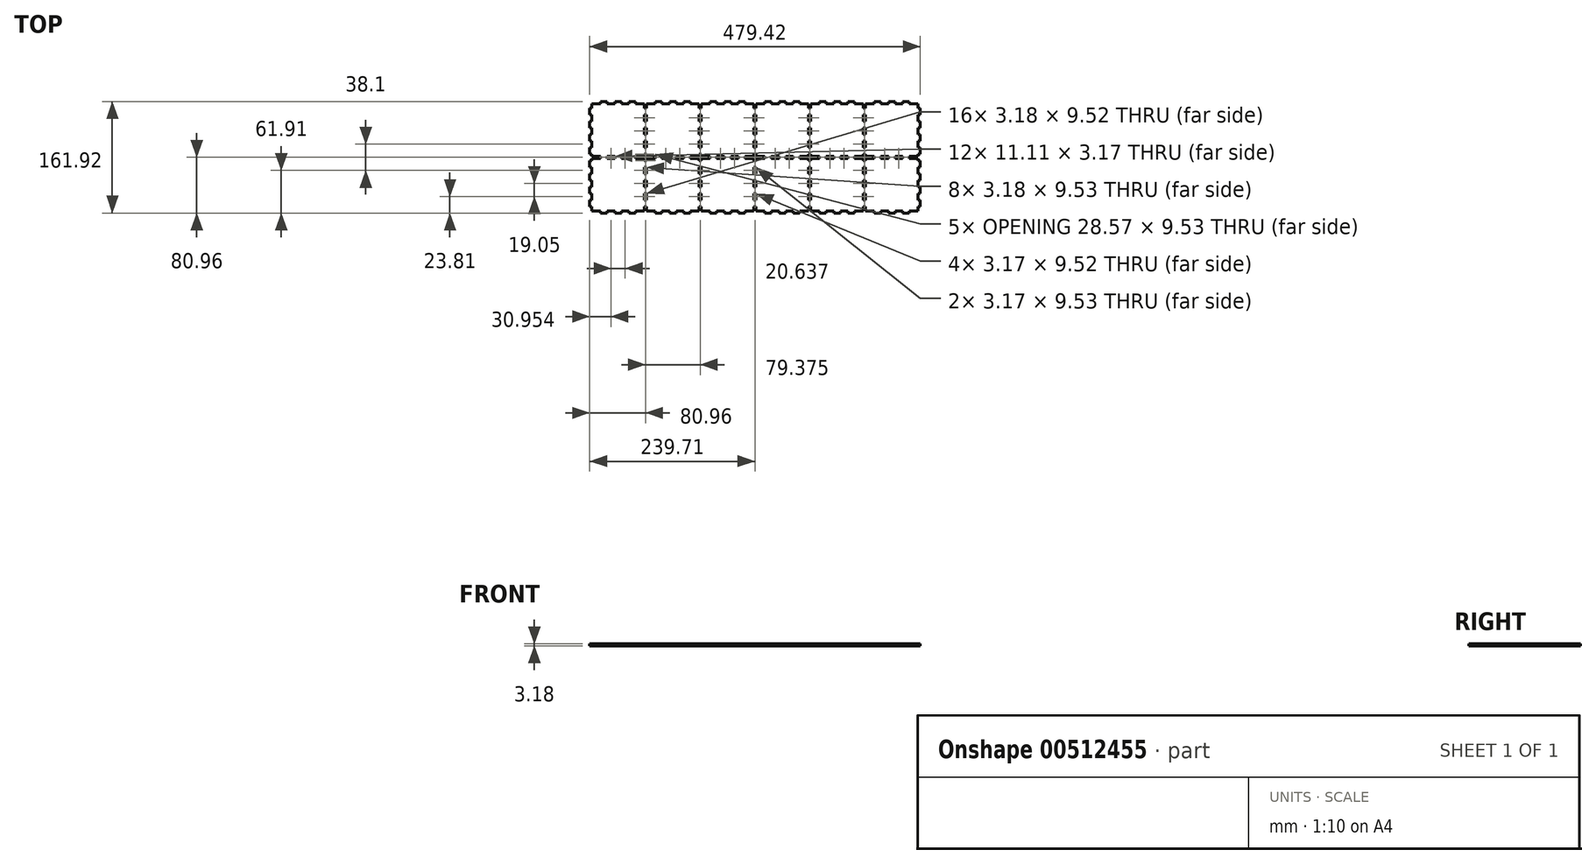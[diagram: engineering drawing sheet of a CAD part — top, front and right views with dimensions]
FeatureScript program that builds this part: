
annotation { "Feature Type Name" : "Feature", "Feature Type Description" : "" }
export const myFeature = defineFeature(function(context is Context, id is Id, definition is map)
    precondition{}
    {
        {
            var Q0;
            Q0=qCreatedBy(makeId("Top.planeOp"),FACE);
            var sketch = newSketch(context, id + "F0", { "sketchPlane" : qUnion([Q0])});
            skLineSegment(sketch, "E0.bottom", {"start": v(-239.71, 80.96) * mm, "end": v(239.71, 80.96) * mm});
            skLineSegment(sketch, "E0.top", {"start": v(-239.71, -80.96) * mm, "end": v(239.71, -80.96) * mm});
            skLineSegment(sketch, "E0.left", {"start": v(-239.71, 80.96) * mm, "end": v(-239.71, -80.96) * mm});
            skLineSegment(sketch, "E0.right", {"start": v(239.71, 80.96) * mm, "end": v(239.71, -80.96) * mm});
            skSolve(sketch);
        }
        {
            var Q0;
            Q0 = qSketchRegion(id + "F0", true);
            extrude(context, id + "F1", {"entities" : qUnion([Q0]), "depth" : 3.17 * mm});
        }
        {
            var Q0;
            Q0=makeQuery(id+"F1.opExtrude","CAP_FACE",FACE,{"disambiguationData":[OSD([sQuery(id+"F0.wireOp",EDGE,"E0.bottom"),sQuery(id+"F0.wireOp",EDGE,"E0.top"),sQuery(id+"F0.wireOp",EDGE,"E0.left"),sQuery(id+"F0.wireOp",EDGE,"E0.right")])],"isStart":false});
            var sketch = newSketch(context, id + "F2", { "sketchPlane" : qUnion([Q0])});
            skLineSegment(sketch, "E1.bottom", {"start": v(-239.71, 80.96) * mm, "end": v(-236.54, 80.96) * mm});
            skLineSegment(sketch, "E1.top", {"start": v(-239.71, 71.44) * mm, "end": v(-236.54, 71.44) * mm});
            skLineSegment(sketch, "E1.left", {"start": v(-239.71, 80.96) * mm, "end": v(-239.71, 71.44) * mm});
            skLineSegment(sketch, "E1.right", {"start": v(-236.54, 80.96) * mm, "end": v(-236.54, 71.44) * mm});
            skLineSegment(sketch, "E2.0.1.0", {"start": v(-239.71, 61.91) * mm, "end": v(-239.71, 52.39) * mm});
            skLineSegment(sketch, "E2.0.1.1", {"start": v(-236.54, 61.91) * mm, "end": v(-236.54, 52.39) * mm});
            skLineSegment(sketch, "E2.0.1.2", {"start": v(-239.71, 61.91) * mm, "end": v(-236.54, 61.91) * mm});
            skLineSegment(sketch, "E2.0.1.3", {"start": v(-239.71, 52.39) * mm, "end": v(-236.54, 52.39) * mm});
            skLineSegment(sketch, "E2.0.2.0", {"start": v(-239.71, 42.86) * mm, "end": v(-239.71, 33.34) * mm});
            skLineSegment(sketch, "E2.0.2.1", {"start": v(-236.54, 42.86) * mm, "end": v(-236.54, 33.34) * mm});
            skLineSegment(sketch, "E2.0.2.2", {"start": v(-239.71, 42.86) * mm, "end": v(-236.54, 42.86) * mm});
            skLineSegment(sketch, "E2.0.2.3", {"start": v(-239.71, 33.34) * mm, "end": v(-236.54, 33.34) * mm});
            skLineSegment(sketch, "E2.0.3.0", {"start": v(-239.71, 23.81) * mm, "end": v(-239.71, 14.29) * mm});
            skLineSegment(sketch, "E2.0.3.1", {"start": v(-236.54, 23.81) * mm, "end": v(-236.54, 14.29) * mm});
            skLineSegment(sketch, "E2.0.3.2", {"start": v(-239.71, 23.81) * mm, "end": v(-236.54, 23.81) * mm});
            skLineSegment(sketch, "E2.0.3.3", {"start": v(-239.71, 14.29) * mm, "end": v(-236.54, 14.29) * mm});
            skLineSegment(sketch, "E2.0.4.0", {"start": v(-239.71, 4.76) * mm, "end": v(-239.71, -4.76) * mm});
            skLineSegment(sketch, "E2.0.4.1", {"start": v(-236.54, 4.76) * mm, "end": v(-236.54, -4.76) * mm});
            skLineSegment(sketch, "E2.0.4.2", {"start": v(-239.71, 4.76) * mm, "end": v(-236.54, 4.76) * mm});
            skLineSegment(sketch, "E2.0.4.3", {"start": v(-239.71, -4.76) * mm, "end": v(-236.54, -4.76) * mm});
            skLineSegment(sketch, "E2.0.5.0", {"start": v(-239.71, -14.29) * mm, "end": v(-239.71, -23.81) * mm});
            skLineSegment(sketch, "E2.0.5.1", {"start": v(-236.54, -14.29) * mm, "end": v(-236.54, -23.81) * mm});
            skLineSegment(sketch, "E2.0.5.2", {"start": v(-239.71, -14.29) * mm, "end": v(-236.54, -14.29) * mm});
            skLineSegment(sketch, "E2.0.5.3", {"start": v(-239.71, -23.81) * mm, "end": v(-236.54, -23.81) * mm});
            skLineSegment(sketch, "E2.0.6.0", {"start": v(-239.71, -33.34) * mm, "end": v(-239.71, -42.86) * mm});
            skLineSegment(sketch, "E2.0.6.1", {"start": v(-236.54, -33.34) * mm, "end": v(-236.54, -42.86) * mm});
            skLineSegment(sketch, "E2.0.6.2", {"start": v(-239.71, -33.34) * mm, "end": v(-236.54, -33.34) * mm});
            skLineSegment(sketch, "E2.0.6.3", {"start": v(-239.71, -42.86) * mm, "end": v(-236.54, -42.86) * mm});
            skLineSegment(sketch, "E2.0.7.0", {"start": v(-239.71, -52.39) * mm, "end": v(-239.71, -61.91) * mm});
            skLineSegment(sketch, "E2.0.7.1", {"start": v(-236.54, -52.39) * mm, "end": v(-236.54, -61.91) * mm});
            skLineSegment(sketch, "E2.0.7.2", {"start": v(-239.71, -52.39) * mm, "end": v(-236.54, -52.39) * mm});
            skLineSegment(sketch, "E2.0.7.3", {"start": v(-239.71, -61.91) * mm, "end": v(-236.54, -61.91) * mm});
            skLineSegment(sketch, "E2.0.8.0", {"start": v(-239.71, -71.44) * mm, "end": v(-239.71, -80.96) * mm});
            skLineSegment(sketch, "E2.0.8.1", {"start": v(-236.54, -71.44) * mm, "end": v(-236.54, -80.96) * mm});
            skLineSegment(sketch, "E2.0.8.2", {"start": v(-239.71, -71.44) * mm, "end": v(-236.54, -71.44) * mm});
            skLineSegment(sketch, "E2.0.8.3", {"start": v(-239.71, -80.96) * mm, "end": v(-236.54, -80.96) * mm});
            skLineSegment(sketch, "E2.direction1", {"start": v(-538.16, 71.44) * mm, "end": v(-239.71, 71.44) * mm, "construction": true});
            skLineSegment(sketch, "E2.direction2", {"start": v(-239.71, 71.44) * mm, "end": v(-239.71, 52.39) * mm, "construction": true});
            skLineSegment(sketch, "E3.1.0.0", {"start": v(-458.79, 71.44) * mm, "end": v(-160.34, 71.44) * mm, "construction": true});
            skLineSegment(sketch, "E3.1.0.1", {"start": v(-160.34, -23.81) * mm, "end": v(-157.16, -23.81) * mm});
            skLineSegment(sketch, "E3.1.0.2", {"start": v(-160.34, -42.86) * mm, "end": v(-157.16, -42.86) * mm});
            skLineSegment(sketch, "E3.1.0.3", {"start": v(-160.34, -14.29) * mm, "end": v(-160.34, -23.81) * mm});
            skLineSegment(sketch, "E3.1.0.4", {"start": v(-157.16, -52.39) * mm, "end": v(-157.16, -61.91) * mm});
            skLineSegment(sketch, "E3.1.0.5", {"start": v(-160.34, -71.44) * mm, "end": v(-160.34, -80.96) * mm});
            skLineSegment(sketch, "E3.1.0.6", {"start": v(-160.34, 4.76) * mm, "end": v(-160.34, -4.76) * mm});
            skLineSegment(sketch, "E3.1.0.7", {"start": v(-160.34, -52.39) * mm, "end": v(-160.34, -61.91) * mm});
            skLineSegment(sketch, "E3.1.0.8", {"start": v(-160.34, -33.34) * mm, "end": v(-160.34, -42.86) * mm});
            skLineSegment(sketch, "E3.1.0.9", {"start": v(-160.34, -52.39) * mm, "end": v(-157.16, -52.39) * mm});
            skLineSegment(sketch, "E3.1.0.10", {"start": v(-160.34, 71.44) * mm, "end": v(-160.34, 52.39) * mm, "construction": true});
            skLineSegment(sketch, "E3.1.0.11", {"start": v(-157.16, -14.29) * mm, "end": v(-157.16, -23.81) * mm});
            skLineSegment(sketch, "E3.1.0.12", {"start": v(-157.16, -71.44) * mm, "end": v(-157.16, -80.96) * mm});
            skLineSegment(sketch, "E3.1.0.13", {"start": v(-157.16, 4.76) * mm, "end": v(-157.16, -4.76) * mm});
            skLineSegment(sketch, "E3.1.0.14", {"start": v(-157.16, 23.81) * mm, "end": v(-157.16, 14.29) * mm});
            skLineSegment(sketch, "E3.1.0.15", {"start": v(-160.34, 23.81) * mm, "end": v(-157.16, 23.81) * mm});
            skLineSegment(sketch, "E3.1.0.16", {"start": v(-160.34, 14.29) * mm, "end": v(-157.16, 14.29) * mm});
            skLineSegment(sketch, "E3.1.0.17", {"start": v(-160.34, 80.96) * mm, "end": v(-157.16, 80.96) * mm});
            skLineSegment(sketch, "E3.1.0.18", {"start": v(-160.34, 80.96) * mm, "end": v(-160.34, 71.44) * mm});
            skLineSegment(sketch, "E3.1.0.19", {"start": v(-157.16, 80.96) * mm, "end": v(-157.16, 71.44) * mm});
            skLineSegment(sketch, "E3.1.0.20", {"start": v(-157.16, 61.91) * mm, "end": v(-157.16, 52.39) * mm});
            skLineSegment(sketch, "E3.1.0.21", {"start": v(-160.34, 61.91) * mm, "end": v(-157.16, 61.91) * mm});
            skLineSegment(sketch, "E3.1.0.22", {"start": v(-160.34, 42.86) * mm, "end": v(-160.34, 33.34) * mm});
            skLineSegment(sketch, "E3.1.0.23", {"start": v(-157.16, 42.86) * mm, "end": v(-157.16, 33.34) * mm});
            skLineSegment(sketch, "E3.1.0.24", {"start": v(-160.34, 42.86) * mm, "end": v(-157.16, 42.86) * mm});
            skLineSegment(sketch, "E3.1.0.25", {"start": v(-160.34, 33.34) * mm, "end": v(-157.16, 33.34) * mm});
            skLineSegment(sketch, "E3.1.0.26", {"start": v(-157.16, -33.34) * mm, "end": v(-157.16, -42.86) * mm});
            skLineSegment(sketch, "E3.1.0.27", {"start": v(-160.34, 23.81) * mm, "end": v(-160.34, 14.29) * mm});
            skLineSegment(sketch, "E3.1.0.28", {"start": v(-160.34, -61.91) * mm, "end": v(-157.16, -61.91) * mm});
            skLineSegment(sketch, "E3.1.0.29", {"start": v(-160.34, -14.29) * mm, "end": v(-157.16, -14.29) * mm});
            skLineSegment(sketch, "E3.1.0.30", {"start": v(-160.34, -71.44) * mm, "end": v(-157.16, -71.44) * mm});
            skLineSegment(sketch, "E3.1.0.31", {"start": v(-160.34, 4.76) * mm, "end": v(-157.16, 4.76) * mm});
            skLineSegment(sketch, "E3.1.0.32", {"start": v(-160.34, -33.34) * mm, "end": v(-157.16, -33.34) * mm});
            skLineSegment(sketch, "E3.1.0.33", {"start": v(-160.34, -80.96) * mm, "end": v(-157.16, -80.96) * mm});
            skLineSegment(sketch, "E3.1.0.34", {"start": v(-160.34, -4.76) * mm, "end": v(-157.16, -4.76) * mm});
            skLineSegment(sketch, "E3.1.0.35", {"start": v(-160.34, 61.91) * mm, "end": v(-160.34, 52.39) * mm});
            skLineSegment(sketch, "E3.1.0.36", {"start": v(-160.34, 52.39) * mm, "end": v(-157.16, 52.39) * mm});
            skLineSegment(sketch, "E3.1.0.37", {"start": v(-160.34, 71.44) * mm, "end": v(-157.16, 71.44) * mm});
            skLineSegment(sketch, "E3.2.0.0", {"start": v(-379.41, 71.44) * mm, "end": v(-80.96, 71.44) * mm, "construction": true});
            skLineSegment(sketch, "E3.2.0.1", {"start": v(-80.96, -23.81) * mm, "end": v(-77.79, -23.81) * mm});
            skLineSegment(sketch, "E3.2.0.2", {"start": v(-80.96, -42.86) * mm, "end": v(-77.79, -42.86) * mm});
            skLineSegment(sketch, "E3.2.0.3", {"start": v(-80.96, -14.29) * mm, "end": v(-80.96, -23.81) * mm});
            skLineSegment(sketch, "E3.2.0.4", {"start": v(-77.79, -52.39) * mm, "end": v(-77.79, -61.91) * mm});
            skLineSegment(sketch, "E3.2.0.5", {"start": v(-80.96, -71.44) * mm, "end": v(-80.96, -80.96) * mm});
            skLineSegment(sketch, "E3.2.0.6", {"start": v(-80.96, 4.76) * mm, "end": v(-80.96, -4.76) * mm});
            skLineSegment(sketch, "E3.2.0.7", {"start": v(-80.96, -52.39) * mm, "end": v(-80.96, -61.91) * mm});
            skLineSegment(sketch, "E3.2.0.8", {"start": v(-80.96, -33.34) * mm, "end": v(-80.96, -42.86) * mm});
            skLineSegment(sketch, "E3.2.0.9", {"start": v(-80.96, -52.39) * mm, "end": v(-77.79, -52.39) * mm});
            skLineSegment(sketch, "E3.2.0.10", {"start": v(-80.96, 71.44) * mm, "end": v(-80.96, 52.39) * mm, "construction": true});
            skLineSegment(sketch, "E3.2.0.11", {"start": v(-77.79, -14.29) * mm, "end": v(-77.79, -23.81) * mm});
            skLineSegment(sketch, "E3.2.0.12", {"start": v(-77.79, -71.44) * mm, "end": v(-77.79, -80.96) * mm});
            skLineSegment(sketch, "E3.2.0.13", {"start": v(-77.79, 4.76) * mm, "end": v(-77.79, -4.76) * mm});
            skLineSegment(sketch, "E3.2.0.14", {"start": v(-77.79, 23.81) * mm, "end": v(-77.79, 14.29) * mm});
            skLineSegment(sketch, "E3.2.0.15", {"start": v(-80.96, 23.81) * mm, "end": v(-77.79, 23.81) * mm});
            skLineSegment(sketch, "E3.2.0.16", {"start": v(-80.96, 14.29) * mm, "end": v(-77.79, 14.29) * mm});
            skLineSegment(sketch, "E3.2.0.17", {"start": v(-80.96, 80.96) * mm, "end": v(-77.79, 80.96) * mm});
            skLineSegment(sketch, "E3.2.0.18", {"start": v(-80.96, 80.96) * mm, "end": v(-80.96, 71.44) * mm});
            skLineSegment(sketch, "E3.2.0.19", {"start": v(-77.79, 80.96) * mm, "end": v(-77.79, 71.44) * mm});
            skLineSegment(sketch, "E3.2.0.20", {"start": v(-77.79, 61.91) * mm, "end": v(-77.79, 52.39) * mm});
            skLineSegment(sketch, "E3.2.0.21", {"start": v(-80.96, 61.91) * mm, "end": v(-77.79, 61.91) * mm});
            skLineSegment(sketch, "E3.2.0.22", {"start": v(-80.96, 42.86) * mm, "end": v(-80.96, 33.34) * mm});
            skLineSegment(sketch, "E3.2.0.23", {"start": v(-77.79, 42.86) * mm, "end": v(-77.79, 33.34) * mm});
            skLineSegment(sketch, "E3.2.0.24", {"start": v(-80.96, 42.86) * mm, "end": v(-77.79, 42.86) * mm});
            skLineSegment(sketch, "E3.2.0.25", {"start": v(-80.96, 33.34) * mm, "end": v(-77.79, 33.34) * mm});
            skLineSegment(sketch, "E3.2.0.26", {"start": v(-77.79, -33.34) * mm, "end": v(-77.79, -42.86) * mm});
            skLineSegment(sketch, "E3.2.0.27", {"start": v(-80.96, 23.81) * mm, "end": v(-80.96, 14.29) * mm});
            skLineSegment(sketch, "E3.2.0.28", {"start": v(-80.96, -61.91) * mm, "end": v(-77.79, -61.91) * mm});
            skLineSegment(sketch, "E3.2.0.29", {"start": v(-80.96, -14.29) * mm, "end": v(-77.79, -14.29) * mm});
            skLineSegment(sketch, "E3.2.0.30", {"start": v(-80.96, -71.44) * mm, "end": v(-77.79, -71.44) * mm});
            skLineSegment(sketch, "E3.2.0.31", {"start": v(-80.96, 4.76) * mm, "end": v(-77.79, 4.76) * mm});
            skLineSegment(sketch, "E3.2.0.32", {"start": v(-80.96, -33.34) * mm, "end": v(-77.79, -33.34) * mm});
            skLineSegment(sketch, "E3.2.0.33", {"start": v(-80.96, -80.96) * mm, "end": v(-77.79, -80.96) * mm});
            skLineSegment(sketch, "E3.2.0.34", {"start": v(-80.96, -4.76) * mm, "end": v(-77.79, -4.76) * mm});
            skLineSegment(sketch, "E3.2.0.35", {"start": v(-80.96, 61.91) * mm, "end": v(-80.96, 52.39) * mm});
            skLineSegment(sketch, "E3.2.0.36", {"start": v(-80.96, 52.39) * mm, "end": v(-77.79, 52.39) * mm});
            skLineSegment(sketch, "E3.2.0.37", {"start": v(-80.96, 71.44) * mm, "end": v(-77.79, 71.44) * mm});
            skLineSegment(sketch, "E3.3.0.0", {"start": v(-300.04, 71.44) * mm, "end": v(-1.59, 71.44) * mm, "construction": true});
            skLineSegment(sketch, "E3.3.0.1", {"start": v(-1.59, -23.81) * mm, "end": v(1.59, -23.81) * mm});
            skLineSegment(sketch, "E3.3.0.2", {"start": v(-1.59, -42.86) * mm, "end": v(1.59, -42.86) * mm});
            skLineSegment(sketch, "E3.3.0.3", {"start": v(-1.59, -14.29) * mm, "end": v(-1.59, -23.81) * mm});
            skLineSegment(sketch, "E3.3.0.4", {"start": v(1.59, -52.39) * mm, "end": v(1.59, -61.91) * mm});
            skLineSegment(sketch, "E3.3.0.5", {"start": v(-1.59, -71.44) * mm, "end": v(-1.59, -80.96) * mm});
            skLineSegment(sketch, "E3.3.0.6", {"start": v(-1.59, 4.76) * mm, "end": v(-1.59, -4.76) * mm});
            skLineSegment(sketch, "E3.3.0.7", {"start": v(-1.59, -52.39) * mm, "end": v(-1.59, -61.91) * mm});
            skLineSegment(sketch, "E3.3.0.8", {"start": v(-1.59, -33.34) * mm, "end": v(-1.59, -42.86) * mm});
            skLineSegment(sketch, "E3.3.0.9", {"start": v(-1.59, -52.39) * mm, "end": v(1.59, -52.39) * mm});
            skLineSegment(sketch, "E3.3.0.10", {"start": v(-1.59, 71.44) * mm, "end": v(-1.59, 52.39) * mm, "construction": true});
            skLineSegment(sketch, "E3.3.0.11", {"start": v(1.59, -14.29) * mm, "end": v(1.59, -23.81) * mm});
            skLineSegment(sketch, "E3.3.0.12", {"start": v(1.59, -71.44) * mm, "end": v(1.59, -80.96) * mm});
            skLineSegment(sketch, "E3.3.0.13", {"start": v(1.59, 4.76) * mm, "end": v(1.59, -4.76) * mm});
            skLineSegment(sketch, "E3.3.0.14", {"start": v(1.59, 23.81) * mm, "end": v(1.59, 14.29) * mm});
            skLineSegment(sketch, "E3.3.0.15", {"start": v(-1.59, 23.81) * mm, "end": v(1.59, 23.81) * mm});
            skLineSegment(sketch, "E3.3.0.16", {"start": v(-1.59, 14.29) * mm, "end": v(1.59, 14.29) * mm});
            skLineSegment(sketch, "E3.3.0.17", {"start": v(-1.59, 80.96) * mm, "end": v(1.59, 80.96) * mm});
            skLineSegment(sketch, "E3.3.0.18", {"start": v(-1.59, 80.96) * mm, "end": v(-1.59, 71.44) * mm});
            skLineSegment(sketch, "E3.3.0.19", {"start": v(1.59, 80.96) * mm, "end": v(1.59, 71.44) * mm});
            skLineSegment(sketch, "E3.3.0.20", {"start": v(1.59, 61.91) * mm, "end": v(1.59, 52.39) * mm});
            skLineSegment(sketch, "E3.3.0.21", {"start": v(-1.59, 61.91) * mm, "end": v(1.59, 61.91) * mm});
            skLineSegment(sketch, "E3.3.0.22", {"start": v(-1.59, 42.86) * mm, "end": v(-1.59, 33.34) * mm});
            skLineSegment(sketch, "E3.3.0.23", {"start": v(1.59, 42.86) * mm, "end": v(1.59, 33.34) * mm});
            skLineSegment(sketch, "E3.3.0.24", {"start": v(-1.59, 42.86) * mm, "end": v(1.59, 42.86) * mm});
            skLineSegment(sketch, "E3.3.0.25", {"start": v(-1.59, 33.34) * mm, "end": v(1.59, 33.34) * mm});
            skLineSegment(sketch, "E3.3.0.26", {"start": v(1.59, -33.34) * mm, "end": v(1.59, -42.86) * mm});
            skLineSegment(sketch, "E3.3.0.27", {"start": v(-1.59, 23.81) * mm, "end": v(-1.59, 14.29) * mm});
            skLineSegment(sketch, "E3.3.0.28", {"start": v(-1.59, -61.91) * mm, "end": v(1.59, -61.91) * mm});
            skLineSegment(sketch, "E3.3.0.29", {"start": v(-1.59, -14.29) * mm, "end": v(1.59, -14.29) * mm});
            skLineSegment(sketch, "E3.3.0.30", {"start": v(-1.59, -71.44) * mm, "end": v(1.59, -71.44) * mm});
            skLineSegment(sketch, "E3.3.0.31", {"start": v(-1.59, 4.76) * mm, "end": v(1.59, 4.76) * mm});
            skLineSegment(sketch, "E3.3.0.32", {"start": v(-1.59, -33.34) * mm, "end": v(1.59, -33.34) * mm});
            skLineSegment(sketch, "E3.3.0.33", {"start": v(-1.59, -80.96) * mm, "end": v(1.59, -80.96) * mm});
            skLineSegment(sketch, "E3.3.0.34", {"start": v(-1.59, -4.76) * mm, "end": v(1.59, -4.76) * mm});
            skLineSegment(sketch, "E3.3.0.35", {"start": v(-1.59, 61.91) * mm, "end": v(-1.59, 52.39) * mm});
            skLineSegment(sketch, "E3.3.0.36", {"start": v(-1.59, 52.39) * mm, "end": v(1.59, 52.39) * mm});
            skLineSegment(sketch, "E3.3.0.37", {"start": v(-1.59, 71.44) * mm, "end": v(1.59, 71.44) * mm});
            skLineSegment(sketch, "E3.4.0.0", {"start": v(-220.66, 71.44) * mm, "end": v(77.79, 71.44) * mm, "construction": true});
            skLineSegment(sketch, "E3.4.0.1", {"start": v(77.79, -23.81) * mm, "end": v(80.96, -23.81) * mm});
            skLineSegment(sketch, "E3.4.0.2", {"start": v(77.79, -42.86) * mm, "end": v(80.96, -42.86) * mm});
            skLineSegment(sketch, "E3.4.0.3", {"start": v(77.79, -14.29) * mm, "end": v(77.79, -23.81) * mm});
            skLineSegment(sketch, "E3.4.0.4", {"start": v(80.96, -52.39) * mm, "end": v(80.96, -61.91) * mm});
            skLineSegment(sketch, "E3.4.0.5", {"start": v(77.79, -71.44) * mm, "end": v(77.79, -80.96) * mm});
            skLineSegment(sketch, "E3.4.0.6", {"start": v(77.79, 4.76) * mm, "end": v(77.79, -4.76) * mm});
            skLineSegment(sketch, "E3.4.0.7", {"start": v(77.79, -52.39) * mm, "end": v(77.79, -61.91) * mm});
            skLineSegment(sketch, "E3.4.0.8", {"start": v(77.79, -33.34) * mm, "end": v(77.79, -42.86) * mm});
            skLineSegment(sketch, "E3.4.0.9", {"start": v(77.79, -52.39) * mm, "end": v(80.96, -52.39) * mm});
            skLineSegment(sketch, "E3.4.0.10", {"start": v(77.79, 71.44) * mm, "end": v(77.79, 52.39) * mm, "construction": true});
            skLineSegment(sketch, "E3.4.0.11", {"start": v(80.96, -14.29) * mm, "end": v(80.96, -23.81) * mm});
            skLineSegment(sketch, "E3.4.0.12", {"start": v(80.96, -71.44) * mm, "end": v(80.96, -80.96) * mm});
            skLineSegment(sketch, "E3.4.0.13", {"start": v(80.96, 4.76) * mm, "end": v(80.96, -4.76) * mm});
            skLineSegment(sketch, "E3.4.0.14", {"start": v(80.96, 23.81) * mm, "end": v(80.96, 14.29) * mm});
            skLineSegment(sketch, "E3.4.0.15", {"start": v(77.79, 23.81) * mm, "end": v(80.96, 23.81) * mm});
            skLineSegment(sketch, "E3.4.0.16", {"start": v(77.79, 14.29) * mm, "end": v(80.96, 14.29) * mm});
            skLineSegment(sketch, "E3.4.0.17", {"start": v(77.79, 80.96) * mm, "end": v(80.96, 80.96) * mm});
            skLineSegment(sketch, "E3.4.0.18", {"start": v(77.79, 80.96) * mm, "end": v(77.79, 71.44) * mm});
            skLineSegment(sketch, "E3.4.0.19", {"start": v(80.96, 80.96) * mm, "end": v(80.96, 71.44) * mm});
            skLineSegment(sketch, "E3.4.0.20", {"start": v(80.96, 61.91) * mm, "end": v(80.96, 52.39) * mm});
            skLineSegment(sketch, "E3.4.0.21", {"start": v(77.79, 61.91) * mm, "end": v(80.96, 61.91) * mm});
            skLineSegment(sketch, "E3.4.0.22", {"start": v(77.79, 42.86) * mm, "end": v(77.79, 33.34) * mm});
            skLineSegment(sketch, "E3.4.0.23", {"start": v(80.96, 42.86) * mm, "end": v(80.96, 33.34) * mm});
            skLineSegment(sketch, "E3.4.0.24", {"start": v(77.79, 42.86) * mm, "end": v(80.96, 42.86) * mm});
            skLineSegment(sketch, "E3.4.0.25", {"start": v(77.79, 33.34) * mm, "end": v(80.96, 33.34) * mm});
            skLineSegment(sketch, "E3.4.0.26", {"start": v(80.96, -33.34) * mm, "end": v(80.96, -42.86) * mm});
            skLineSegment(sketch, "E3.4.0.27", {"start": v(77.79, 23.81) * mm, "end": v(77.79, 14.29) * mm});
            skLineSegment(sketch, "E3.4.0.28", {"start": v(77.79, -61.91) * mm, "end": v(80.96, -61.91) * mm});
            skLineSegment(sketch, "E3.4.0.29", {"start": v(77.79, -14.29) * mm, "end": v(80.96, -14.29) * mm});
            skLineSegment(sketch, "E3.4.0.30", {"start": v(77.79, -71.44) * mm, "end": v(80.96, -71.44) * mm});
            skLineSegment(sketch, "E3.4.0.31", {"start": v(77.79, 4.76) * mm, "end": v(80.96, 4.76) * mm});
            skLineSegment(sketch, "E3.4.0.32", {"start": v(77.79, -33.34) * mm, "end": v(80.96, -33.34) * mm});
            skLineSegment(sketch, "E3.4.0.33", {"start": v(77.79, -80.96) * mm, "end": v(80.96, -80.96) * mm});
            skLineSegment(sketch, "E3.4.0.34", {"start": v(77.79, -4.76) * mm, "end": v(80.96, -4.76) * mm});
            skLineSegment(sketch, "E3.4.0.35", {"start": v(77.79, 61.91) * mm, "end": v(77.79, 52.39) * mm});
            skLineSegment(sketch, "E3.4.0.36", {"start": v(77.79, 52.39) * mm, "end": v(80.96, 52.39) * mm});
            skLineSegment(sketch, "E3.4.0.37", {"start": v(77.79, 71.44) * mm, "end": v(80.96, 71.44) * mm});
            skLineSegment(sketch, "E3.5.0.0", {"start": v(-141.29, 71.44) * mm, "end": v(157.16, 71.44) * mm, "construction": true});
            skLineSegment(sketch, "E3.5.0.1", {"start": v(157.16, -23.81) * mm, "end": v(160.34, -23.81) * mm});
            skLineSegment(sketch, "E3.5.0.2", {"start": v(157.16, -42.86) * mm, "end": v(160.34, -42.86) * mm});
            skLineSegment(sketch, "E3.5.0.3", {"start": v(157.16, -14.29) * mm, "end": v(157.16, -23.81) * mm});
            skLineSegment(sketch, "E3.5.0.4", {"start": v(160.34, -52.39) * mm, "end": v(160.34, -61.91) * mm});
            skLineSegment(sketch, "E3.5.0.5", {"start": v(157.16, -71.44) * mm, "end": v(157.16, -80.96) * mm});
            skLineSegment(sketch, "E3.5.0.6", {"start": v(157.16, 4.76) * mm, "end": v(157.16, -4.76) * mm});
            skLineSegment(sketch, "E3.5.0.7", {"start": v(157.16, -52.39) * mm, "end": v(157.16, -61.91) * mm});
            skLineSegment(sketch, "E3.5.0.8", {"start": v(157.16, -33.34) * mm, "end": v(157.16, -42.86) * mm});
            skLineSegment(sketch, "E3.5.0.9", {"start": v(157.16, -52.39) * mm, "end": v(160.34, -52.39) * mm});
            skLineSegment(sketch, "E3.5.0.10", {"start": v(157.16, 71.44) * mm, "end": v(157.16, 52.39) * mm, "construction": true});
            skLineSegment(sketch, "E3.5.0.11", {"start": v(160.34, -14.29) * mm, "end": v(160.34, -23.81) * mm});
            skLineSegment(sketch, "E3.5.0.12", {"start": v(160.34, -71.44) * mm, "end": v(160.34, -80.96) * mm});
            skLineSegment(sketch, "E3.5.0.13", {"start": v(160.34, 4.76) * mm, "end": v(160.34, -4.76) * mm});
            skLineSegment(sketch, "E3.5.0.14", {"start": v(160.34, 23.81) * mm, "end": v(160.34, 14.29) * mm});
            skLineSegment(sketch, "E3.5.0.15", {"start": v(157.16, 23.81) * mm, "end": v(160.34, 23.81) * mm});
            skLineSegment(sketch, "E3.5.0.16", {"start": v(157.16, 14.29) * mm, "end": v(160.34, 14.29) * mm});
            skLineSegment(sketch, "E3.5.0.17", {"start": v(157.16, 80.96) * mm, "end": v(160.34, 80.96) * mm});
            skLineSegment(sketch, "E3.5.0.18", {"start": v(157.16, 80.96) * mm, "end": v(157.16, 71.44) * mm});
            skLineSegment(sketch, "E3.5.0.19", {"start": v(160.34, 80.96) * mm, "end": v(160.34, 71.44) * mm});
            skLineSegment(sketch, "E3.5.0.20", {"start": v(160.34, 61.91) * mm, "end": v(160.34, 52.39) * mm});
            skLineSegment(sketch, "E3.5.0.21", {"start": v(157.16, 61.91) * mm, "end": v(160.34, 61.91) * mm});
            skLineSegment(sketch, "E3.5.0.22", {"start": v(157.16, 42.86) * mm, "end": v(157.16, 33.34) * mm});
            skLineSegment(sketch, "E3.5.0.23", {"start": v(160.34, 42.86) * mm, "end": v(160.34, 33.34) * mm});
            skLineSegment(sketch, "E3.5.0.24", {"start": v(157.16, 42.86) * mm, "end": v(160.34, 42.86) * mm});
            skLineSegment(sketch, "E3.5.0.25", {"start": v(157.16, 33.34) * mm, "end": v(160.34, 33.34) * mm});
            skLineSegment(sketch, "E3.5.0.26", {"start": v(160.34, -33.34) * mm, "end": v(160.34, -42.86) * mm});
            skLineSegment(sketch, "E3.5.0.27", {"start": v(157.16, 23.81) * mm, "end": v(157.16, 14.29) * mm});
            skLineSegment(sketch, "E3.5.0.28", {"start": v(157.16, -61.91) * mm, "end": v(160.34, -61.91) * mm});
            skLineSegment(sketch, "E3.5.0.29", {"start": v(157.16, -14.29) * mm, "end": v(160.34, -14.29) * mm});
            skLineSegment(sketch, "E3.5.0.30", {"start": v(157.16, -71.44) * mm, "end": v(160.34, -71.44) * mm});
            skLineSegment(sketch, "E3.5.0.31", {"start": v(157.16, 4.76) * mm, "end": v(160.34, 4.76) * mm});
            skLineSegment(sketch, "E3.5.0.32", {"start": v(157.16, -33.34) * mm, "end": v(160.34, -33.34) * mm});
            skLineSegment(sketch, "E3.5.0.33", {"start": v(157.16, -80.96) * mm, "end": v(160.34, -80.96) * mm});
            skLineSegment(sketch, "E3.5.0.34", {"start": v(157.16, -4.76) * mm, "end": v(160.34, -4.76) * mm});
            skLineSegment(sketch, "E3.5.0.35", {"start": v(157.16, 61.91) * mm, "end": v(157.16, 52.39) * mm});
            skLineSegment(sketch, "E3.5.0.36", {"start": v(157.16, 52.39) * mm, "end": v(160.34, 52.39) * mm});
            skLineSegment(sketch, "E3.5.0.37", {"start": v(157.16, 71.44) * mm, "end": v(160.34, 71.44) * mm});
            skLineSegment(sketch, "E3.6.0.0", {"start": v(-61.91, 71.44) * mm, "end": v(236.54, 71.44) * mm, "construction": true});
            skLineSegment(sketch, "E3.6.0.1", {"start": v(236.54, -23.81) * mm, "end": v(239.71, -23.81) * mm});
            skLineSegment(sketch, "E3.6.0.2", {"start": v(236.54, -42.86) * mm, "end": v(239.71, -42.86) * mm});
            skLineSegment(sketch, "E3.6.0.3", {"start": v(236.54, -14.29) * mm, "end": v(236.54, -23.81) * mm});
            skLineSegment(sketch, "E3.6.0.4", {"start": v(239.71, -52.39) * mm, "end": v(239.71, -61.91) * mm});
            skLineSegment(sketch, "E3.6.0.5", {"start": v(236.54, -71.44) * mm, "end": v(236.54, -80.96) * mm});
            skLineSegment(sketch, "E3.6.0.6", {"start": v(236.54, 4.76) * mm, "end": v(236.54, -4.76) * mm});
            skLineSegment(sketch, "E3.6.0.7", {"start": v(236.54, -52.39) * mm, "end": v(236.54, -61.91) * mm});
            skLineSegment(sketch, "E3.6.0.8", {"start": v(236.54, -33.34) * mm, "end": v(236.54, -42.86) * mm});
            skLineSegment(sketch, "E3.6.0.9", {"start": v(236.54, -52.39) * mm, "end": v(239.71, -52.39) * mm});
            skLineSegment(sketch, "E3.6.0.10", {"start": v(236.54, 71.44) * mm, "end": v(236.54, 52.39) * mm, "construction": true});
            skLineSegment(sketch, "E3.6.0.11", {"start": v(239.71, -14.29) * mm, "end": v(239.71, -23.81) * mm});
            skLineSegment(sketch, "E3.6.0.12", {"start": v(239.71, -71.44) * mm, "end": v(239.71, -80.96) * mm});
            skLineSegment(sketch, "E3.6.0.13", {"start": v(239.71, 4.76) * mm, "end": v(239.71, -4.76) * mm});
            skLineSegment(sketch, "E3.6.0.14", {"start": v(239.71, 23.81) * mm, "end": v(239.71, 14.29) * mm});
            skLineSegment(sketch, "E3.6.0.15", {"start": v(236.54, 23.81) * mm, "end": v(239.71, 23.81) * mm});
            skLineSegment(sketch, "E3.6.0.16", {"start": v(236.54, 14.29) * mm, "end": v(239.71, 14.29) * mm});
            skLineSegment(sketch, "E3.6.0.17", {"start": v(236.54, 80.96) * mm, "end": v(239.71, 80.96) * mm});
            skLineSegment(sketch, "E3.6.0.18", {"start": v(236.54, 80.96) * mm, "end": v(236.54, 71.44) * mm});
            skLineSegment(sketch, "E3.6.0.19", {"start": v(239.71, 80.96) * mm, "end": v(239.71, 71.44) * mm});
            skLineSegment(sketch, "E3.6.0.20", {"start": v(239.71, 61.91) * mm, "end": v(239.71, 52.39) * mm});
            skLineSegment(sketch, "E3.6.0.21", {"start": v(236.54, 61.91) * mm, "end": v(239.71, 61.91) * mm});
            skLineSegment(sketch, "E3.6.0.22", {"start": v(236.54, 42.86) * mm, "end": v(236.54, 33.34) * mm});
            skLineSegment(sketch, "E3.6.0.23", {"start": v(239.71, 42.86) * mm, "end": v(239.71, 33.34) * mm});
            skLineSegment(sketch, "E3.6.0.24", {"start": v(236.54, 42.86) * mm, "end": v(239.71, 42.86) * mm});
            skLineSegment(sketch, "E3.6.0.25", {"start": v(236.54, 33.34) * mm, "end": v(239.71, 33.34) * mm});
            skLineSegment(sketch, "E3.6.0.26", {"start": v(239.71, -33.34) * mm, "end": v(239.71, -42.86) * mm});
            skLineSegment(sketch, "E3.6.0.27", {"start": v(236.54, 23.81) * mm, "end": v(236.54, 14.29) * mm});
            skLineSegment(sketch, "E3.6.0.28", {"start": v(236.54, -61.91) * mm, "end": v(239.71, -61.91) * mm});
            skLineSegment(sketch, "E3.6.0.29", {"start": v(236.54, -14.29) * mm, "end": v(239.71, -14.29) * mm});
            skLineSegment(sketch, "E3.6.0.30", {"start": v(236.54, -71.44) * mm, "end": v(239.71, -71.44) * mm});
            skLineSegment(sketch, "E3.6.0.31", {"start": v(236.54, 4.76) * mm, "end": v(239.71, 4.76) * mm});
            skLineSegment(sketch, "E3.6.0.32", {"start": v(236.54, -33.34) * mm, "end": v(239.71, -33.34) * mm});
            skLineSegment(sketch, "E3.6.0.33", {"start": v(236.54, -80.96) * mm, "end": v(239.71, -80.96) * mm});
            skLineSegment(sketch, "E3.6.0.34", {"start": v(236.54, -4.76) * mm, "end": v(239.71, -4.76) * mm});
            skLineSegment(sketch, "E3.6.0.35", {"start": v(236.54, 61.91) * mm, "end": v(236.54, 52.39) * mm});
            skLineSegment(sketch, "E3.6.0.36", {"start": v(236.54, 52.39) * mm, "end": v(239.71, 52.39) * mm});
            skLineSegment(sketch, "E3.6.0.37", {"start": v(236.54, 71.44) * mm, "end": v(239.71, 71.44) * mm});
            skLineSegment(sketch, "E3.direction1", {"start": v(-239.71, -80.96) * mm, "end": v(-160.34, -80.96) * mm, "construction": true});
            skSolve(sketch);
        }
        {
            var Q0;
            Q0 = qSketchRegion(id + "F2", true);
            extrude(context, id + "F3", {"entities" : qUnion([Q0]), "operationType" : NewBodyOperationType.REMOVE, "endBound" : BoundingType.THROUGH_ALL, "oppositeDirection" : true, "depth" : 25.4 * mm});
        }
        {
            var Q0;
            Q0=makeQuery(id+"F1.opExtrude","CAP_FACE",FACE,{"disambiguationData":[OSD([sQuery(id+"F0.wireOp",EDGE,"E0.bottom"),sQuery(id+"F0.wireOp",EDGE,"E0.top"),sQuery(id+"F0.wireOp",EDGE,"E0.left"),sQuery(id+"F0.wireOp",EDGE,"E0.right")])],"isStart":false});
            var sketch = newSketch(context, id + "F4", { "sketchPlane" : qUnion([Q0])});
            skLineSegment(sketch, "E4.bottom", {"start": v(-236.54, 80.96) * mm, "end": v(-223.84, 80.96) * mm});
            skLineSegment(sketch, "E4.top", {"start": v(-236.54, 77.79) * mm, "end": v(-223.84, 77.79) * mm});
            skLineSegment(sketch, "E4.left", {"start": v(-236.54, 80.96) * mm, "end": v(-236.54, 77.79) * mm});
            skLineSegment(sketch, "E4.right", {"start": v(-223.84, 80.96) * mm, "end": v(-223.84, 77.79) * mm});
            skLineSegment(sketch, "E5.bottom", {"start": v(-214.31, 80.96) * mm, "end": v(-203.2, 80.96) * mm});
            skLineSegment(sketch, "E5.top", {"start": v(-214.31, 77.79) * mm, "end": v(-203.2, 77.79) * mm});
            skLineSegment(sketch, "E5.left", {"start": v(-214.31, 80.96) * mm, "end": v(-214.31, 77.79) * mm});
            skLineSegment(sketch, "E5.right", {"start": v(-203.2, 80.96) * mm, "end": v(-203.2, 77.79) * mm});
            skLineSegment(sketch, "E6.1.0.0", {"start": v(-193.68, 77.79) * mm, "end": v(-182.56, 77.79) * mm});
            skLineSegment(sketch, "E6.1.0.1", {"start": v(-182.56, 80.96) * mm, "end": v(-182.56, 77.79) * mm});
            skLineSegment(sketch, "E6.1.0.2", {"start": v(-193.68, 80.96) * mm, "end": v(-193.68, 77.79) * mm});
            skLineSegment(sketch, "E6.1.0.3", {"start": v(-193.68, 80.96) * mm, "end": v(-182.56, 80.96) * mm});
            skLineSegment(sketch, "E6.direction1", {"start": v(-214.31, 77.79) * mm, "end": v(-193.68, 77.79) * mm, "construction": true});
            skLineSegment(sketch, "E7.bottom", {"start": v(-160.34, 80.96) * mm, "end": v(-173.04, 80.96) * mm});
            skLineSegment(sketch, "E7.top", {"start": v(-160.34, 77.79) * mm, "end": v(-173.04, 77.79) * mm});
            skLineSegment(sketch, "E7.left", {"start": v(-160.34, 80.96) * mm, "end": v(-160.34, 77.79) * mm});
            skLineSegment(sketch, "E7.right", {"start": v(-173.04, 80.96) * mm, "end": v(-173.04, 77.79) * mm});
            skLineSegment(sketch, "E8.0.1.0", {"start": v(-214.31, 1.59) * mm, "end": v(-203.2, 1.59) * mm});
            skLineSegment(sketch, "E8.0.1.1", {"start": v(-193.68, -1.59) * mm, "end": v(-182.56, -1.59) * mm});
            skLineSegment(sketch, "E8.0.1.2", {"start": v(-214.31, -1.59) * mm, "end": v(-193.68, -1.59) * mm, "construction": true});
            skLineSegment(sketch, "E8.0.1.3", {"start": v(-193.68, 1.59) * mm, "end": v(-182.56, 1.59) * mm});
            skLineSegment(sketch, "E8.0.1.4", {"start": v(-160.34, -1.59) * mm, "end": v(-173.04, -1.59) * mm});
            skLineSegment(sketch, "E8.0.1.5", {"start": v(-236.54, -1.59) * mm, "end": v(-223.84, -1.59) * mm});
            skLineSegment(sketch, "E8.0.1.6", {"start": v(-236.54, 1.59) * mm, "end": v(-223.84, 1.59) * mm});
            skLineSegment(sketch, "E8.0.1.7", {"start": v(-160.34, 1.59) * mm, "end": v(-173.04, 1.59) * mm});
            skLineSegment(sketch, "E8.0.1.8", {"start": v(-214.31, -1.59) * mm, "end": v(-203.2, -1.59) * mm});
            skLineSegment(sketch, "E8.0.1.9", {"start": v(-203.2, 1.59) * mm, "end": v(-203.2, -1.59) * mm});
            skLineSegment(sketch, "E8.0.1.10", {"start": v(-193.68, 1.59) * mm, "end": v(-193.68, -1.59) * mm});
            skLineSegment(sketch, "E8.0.1.11", {"start": v(-214.31, 1.59) * mm, "end": v(-214.31, -1.59) * mm});
            skLineSegment(sketch, "E8.0.1.12", {"start": v(-236.54, 1.59) * mm, "end": v(-236.54, -1.59) * mm});
            skLineSegment(sketch, "E8.0.1.13", {"start": v(-173.04, 1.59) * mm, "end": v(-173.04, -1.59) * mm});
            skLineSegment(sketch, "E8.0.1.14", {"start": v(-223.84, 1.59) * mm, "end": v(-223.84, -1.59) * mm});
            skLineSegment(sketch, "E8.0.1.15", {"start": v(-160.34, 1.59) * mm, "end": v(-160.34, -1.59) * mm});
            skLineSegment(sketch, "E8.0.1.16", {"start": v(-182.56, 1.59) * mm, "end": v(-182.56, -1.59) * mm});
            skLineSegment(sketch, "E8.0.2.0", {"start": v(-214.31, -77.79) * mm, "end": v(-203.2, -77.79) * mm});
            skLineSegment(sketch, "E8.0.2.1", {"start": v(-193.68, -80.96) * mm, "end": v(-182.56, -80.96) * mm});
            skLineSegment(sketch, "E8.0.2.2", {"start": v(-214.31, -80.96) * mm, "end": v(-193.68, -80.96) * mm, "construction": true});
            skLineSegment(sketch, "E8.0.2.3", {"start": v(-193.68, -77.79) * mm, "end": v(-182.56, -77.79) * mm});
            skLineSegment(sketch, "E8.0.2.4", {"start": v(-160.34, -80.96) * mm, "end": v(-173.04, -80.96) * mm});
            skLineSegment(sketch, "E8.0.2.5", {"start": v(-236.54, -80.96) * mm, "end": v(-223.84, -80.96) * mm});
            skLineSegment(sketch, "E8.0.2.6", {"start": v(-236.54, -77.79) * mm, "end": v(-223.84, -77.79) * mm});
            skLineSegment(sketch, "E8.0.2.7", {"start": v(-160.34, -77.79) * mm, "end": v(-173.04, -77.79) * mm});
            skLineSegment(sketch, "E8.0.2.8", {"start": v(-214.31, -80.96) * mm, "end": v(-203.2, -80.96) * mm});
            skLineSegment(sketch, "E8.0.2.9", {"start": v(-203.2, -77.79) * mm, "end": v(-203.2, -80.96) * mm});
            skLineSegment(sketch, "E8.0.2.10", {"start": v(-193.68, -77.79) * mm, "end": v(-193.68, -80.96) * mm});
            skLineSegment(sketch, "E8.0.2.11", {"start": v(-214.31, -77.79) * mm, "end": v(-214.31, -80.96) * mm});
            skLineSegment(sketch, "E8.0.2.12", {"start": v(-236.54, -77.79) * mm, "end": v(-236.54, -80.96) * mm});
            skLineSegment(sketch, "E8.0.2.13", {"start": v(-173.04, -77.79) * mm, "end": v(-173.04, -80.96) * mm});
            skLineSegment(sketch, "E8.0.2.14", {"start": v(-223.84, -77.79) * mm, "end": v(-223.84, -80.96) * mm});
            skLineSegment(sketch, "E8.0.2.15", {"start": v(-160.34, -77.79) * mm, "end": v(-160.34, -80.96) * mm});
            skLineSegment(sketch, "E8.0.2.16", {"start": v(-182.56, -77.79) * mm, "end": v(-182.56, -80.96) * mm});
            skLineSegment(sketch, "E8.1.0.0", {"start": v(-134.94, 80.96) * mm, "end": v(-123.83, 80.96) * mm});
            skLineSegment(sketch, "E8.1.0.1", {"start": v(-114.3, 77.79) * mm, "end": v(-103.19, 77.79) * mm});
            skLineSegment(sketch, "E8.1.0.2", {"start": v(-134.94, 77.79) * mm, "end": v(-114.3, 77.79) * mm, "construction": true});
            skLineSegment(sketch, "E8.1.0.3", {"start": v(-114.3, 80.96) * mm, "end": v(-103.19, 80.96) * mm});
            skLineSegment(sketch, "E8.1.0.4", {"start": v(-80.96, 77.79) * mm, "end": v(-93.66, 77.79) * mm});
            skLineSegment(sketch, "E8.1.0.5", {"start": v(-157.16, 77.79) * mm, "end": v(-144.46, 77.79) * mm});
            skLineSegment(sketch, "E8.1.0.6", {"start": v(-157.16, 80.96) * mm, "end": v(-144.46, 80.96) * mm});
            skLineSegment(sketch, "E8.1.0.7", {"start": v(-80.96, 80.96) * mm, "end": v(-93.66, 80.96) * mm});
            skLineSegment(sketch, "E8.1.0.8", {"start": v(-134.94, 77.79) * mm, "end": v(-123.83, 77.79) * mm});
            skLineSegment(sketch, "E8.1.0.9", {"start": v(-123.83, 80.96) * mm, "end": v(-123.83, 77.79) * mm});
            skLineSegment(sketch, "E8.1.0.10", {"start": v(-114.3, 80.96) * mm, "end": v(-114.3, 77.79) * mm});
            skLineSegment(sketch, "E8.1.0.11", {"start": v(-134.94, 80.96) * mm, "end": v(-134.94, 77.79) * mm});
            skLineSegment(sketch, "E8.1.0.12", {"start": v(-157.16, 80.96) * mm, "end": v(-157.16, 77.79) * mm});
            skLineSegment(sketch, "E8.1.0.13", {"start": v(-93.66, 80.96) * mm, "end": v(-93.66, 77.79) * mm});
            skLineSegment(sketch, "E8.1.0.14", {"start": v(-144.46, 80.96) * mm, "end": v(-144.46, 77.79) * mm});
            skLineSegment(sketch, "E8.1.0.15", {"start": v(-80.96, 80.96) * mm, "end": v(-80.96, 77.79) * mm});
            skLineSegment(sketch, "E8.1.0.16", {"start": v(-103.19, 80.96) * mm, "end": v(-103.19, 77.79) * mm});
            skLineSegment(sketch, "E8.1.1.0", {"start": v(-134.94, 1.59) * mm, "end": v(-123.83, 1.59) * mm});
            skLineSegment(sketch, "E8.1.1.1", {"start": v(-114.3, -1.59) * mm, "end": v(-103.19, -1.59) * mm});
            skLineSegment(sketch, "E8.1.1.2", {"start": v(-134.94, -1.59) * mm, "end": v(-114.3, -1.59) * mm, "construction": true});
            skLineSegment(sketch, "E8.1.1.3", {"start": v(-114.3, 1.59) * mm, "end": v(-103.19, 1.59) * mm});
            skLineSegment(sketch, "E8.1.1.4", {"start": v(-80.96, -1.59) * mm, "end": v(-93.66, -1.59) * mm});
            skLineSegment(sketch, "E8.1.1.5", {"start": v(-157.16, -1.59) * mm, "end": v(-144.46, -1.59) * mm});
            skLineSegment(sketch, "E8.1.1.6", {"start": v(-157.16, 1.59) * mm, "end": v(-144.46, 1.59) * mm});
            skLineSegment(sketch, "E8.1.1.7", {"start": v(-80.96, 1.59) * mm, "end": v(-93.66, 1.59) * mm});
            skLineSegment(sketch, "E8.1.1.8", {"start": v(-134.94, -1.59) * mm, "end": v(-123.83, -1.59) * mm});
            skLineSegment(sketch, "E8.1.1.9", {"start": v(-123.83, 1.59) * mm, "end": v(-123.83, -1.59) * mm});
            skLineSegment(sketch, "E8.1.1.10", {"start": v(-114.3, 1.59) * mm, "end": v(-114.3, -1.59) * mm});
            skLineSegment(sketch, "E8.1.1.11", {"start": v(-134.94, 1.59) * mm, "end": v(-134.94, -1.59) * mm});
            skLineSegment(sketch, "E8.1.1.12", {"start": v(-157.16, 1.59) * mm, "end": v(-157.16, -1.59) * mm});
            skLineSegment(sketch, "E8.1.1.13", {"start": v(-93.66, 1.59) * mm, "end": v(-93.66, -1.59) * mm});
            skLineSegment(sketch, "E8.1.1.14", {"start": v(-144.46, 1.59) * mm, "end": v(-144.46, -1.59) * mm});
            skLineSegment(sketch, "E8.1.1.15", {"start": v(-80.96, 1.59) * mm, "end": v(-80.96, -1.59) * mm});
            skLineSegment(sketch, "E8.1.1.16", {"start": v(-103.19, 1.59) * mm, "end": v(-103.19, -1.59) * mm});
            skLineSegment(sketch, "E8.1.2.0", {"start": v(-134.94, -77.79) * mm, "end": v(-123.83, -77.79) * mm});
            skLineSegment(sketch, "E8.1.2.1", {"start": v(-114.3, -80.96) * mm, "end": v(-103.19, -80.96) * mm});
            skLineSegment(sketch, "E8.1.2.2", {"start": v(-134.94, -80.96) * mm, "end": v(-114.3, -80.96) * mm, "construction": true});
            skLineSegment(sketch, "E8.1.2.3", {"start": v(-114.3, -77.79) * mm, "end": v(-103.19, -77.79) * mm});
            skLineSegment(sketch, "E8.1.2.4", {"start": v(-80.96, -80.96) * mm, "end": v(-93.66, -80.96) * mm});
            skLineSegment(sketch, "E8.1.2.5", {"start": v(-157.16, -80.96) * mm, "end": v(-144.46, -80.96) * mm});
            skLineSegment(sketch, "E8.1.2.6", {"start": v(-157.16, -77.79) * mm, "end": v(-144.46, -77.79) * mm});
            skLineSegment(sketch, "E8.1.2.7", {"start": v(-80.96, -77.79) * mm, "end": v(-93.66, -77.79) * mm});
            skLineSegment(sketch, "E8.1.2.8", {"start": v(-134.94, -80.96) * mm, "end": v(-123.83, -80.96) * mm});
            skLineSegment(sketch, "E8.1.2.9", {"start": v(-123.83, -77.79) * mm, "end": v(-123.83, -80.96) * mm});
            skLineSegment(sketch, "E8.1.2.10", {"start": v(-114.3, -77.79) * mm, "end": v(-114.3, -80.96) * mm});
            skLineSegment(sketch, "E8.1.2.11", {"start": v(-134.94, -77.79) * mm, "end": v(-134.94, -80.96) * mm});
            skLineSegment(sketch, "E8.1.2.12", {"start": v(-157.16, -77.79) * mm, "end": v(-157.16, -80.96) * mm});
            skLineSegment(sketch, "E8.1.2.13", {"start": v(-93.66, -77.79) * mm, "end": v(-93.66, -80.96) * mm});
            skLineSegment(sketch, "E8.1.2.14", {"start": v(-144.46, -77.79) * mm, "end": v(-144.46, -80.96) * mm});
            skLineSegment(sketch, "E8.1.2.15", {"start": v(-80.96, -77.79) * mm, "end": v(-80.96, -80.96) * mm});
            skLineSegment(sketch, "E8.1.2.16", {"start": v(-103.19, -77.79) * mm, "end": v(-103.19, -80.96) * mm});
            skLineSegment(sketch, "E8.2.0.0", {"start": v(-55.56, 80.96) * mm, "end": v(-44.45, 80.96) * mm});
            skLineSegment(sketch, "E8.2.0.1", {"start": v(-34.93, 77.79) * mm, "end": v(-23.81, 77.79) * mm});
            skLineSegment(sketch, "E8.2.0.2", {"start": v(-55.56, 77.79) * mm, "end": v(-34.93, 77.79) * mm, "construction": true});
            skLineSegment(sketch, "E8.2.0.3", {"start": v(-34.93, 80.96) * mm, "end": v(-23.81, 80.96) * mm});
            skLineSegment(sketch, "E8.2.0.4", {"start": v(-1.59, 77.79) * mm, "end": v(-14.29, 77.79) * mm});
            skLineSegment(sketch, "E8.2.0.5", {"start": v(-77.79, 77.79) * mm, "end": v(-65.09, 77.79) * mm});
            skLineSegment(sketch, "E8.2.0.6", {"start": v(-77.79, 80.96) * mm, "end": v(-65.09, 80.96) * mm});
            skLineSegment(sketch, "E8.2.0.7", {"start": v(-1.59, 80.96) * mm, "end": v(-14.29, 80.96) * mm});
            skLineSegment(sketch, "E8.2.0.8", {"start": v(-55.56, 77.79) * mm, "end": v(-44.45, 77.79) * mm});
            skLineSegment(sketch, "E8.2.0.9", {"start": v(-44.45, 80.96) * mm, "end": v(-44.45, 77.79) * mm});
            skLineSegment(sketch, "E8.2.0.10", {"start": v(-34.93, 80.96) * mm, "end": v(-34.93, 77.79) * mm});
            skLineSegment(sketch, "E8.2.0.11", {"start": v(-55.56, 80.96) * mm, "end": v(-55.56, 77.79) * mm});
            skLineSegment(sketch, "E8.2.0.12", {"start": v(-77.79, 80.96) * mm, "end": v(-77.79, 77.79) * mm});
            skLineSegment(sketch, "E8.2.0.13", {"start": v(-14.29, 80.96) * mm, "end": v(-14.29, 77.79) * mm});
            skLineSegment(sketch, "E8.2.0.14", {"start": v(-65.09, 80.96) * mm, "end": v(-65.09, 77.79) * mm});
            skLineSegment(sketch, "E8.2.0.15", {"start": v(-1.59, 80.96) * mm, "end": v(-1.59, 77.79) * mm});
            skLineSegment(sketch, "E8.2.0.16", {"start": v(-23.81, 80.96) * mm, "end": v(-23.81, 77.79) * mm});
            skLineSegment(sketch, "E8.2.1.0", {"start": v(-55.56, 1.59) * mm, "end": v(-44.45, 1.59) * mm});
            skLineSegment(sketch, "E8.2.1.1", {"start": v(-34.93, -1.59) * mm, "end": v(-23.81, -1.59) * mm});
            skLineSegment(sketch, "E8.2.1.2", {"start": v(-55.56, -1.59) * mm, "end": v(-34.93, -1.59) * mm, "construction": true});
            skLineSegment(sketch, "E8.2.1.3", {"start": v(-34.93, 1.59) * mm, "end": v(-23.81, 1.59) * mm});
            skLineSegment(sketch, "E8.2.1.4", {"start": v(-1.59, -1.59) * mm, "end": v(-14.29, -1.59) * mm});
            skLineSegment(sketch, "E8.2.1.5", {"start": v(-77.79, -1.59) * mm, "end": v(-65.09, -1.59) * mm});
            skLineSegment(sketch, "E8.2.1.6", {"start": v(-77.79, 1.59) * mm, "end": v(-65.09, 1.59) * mm});
            skLineSegment(sketch, "E8.2.1.7", {"start": v(-1.59, 1.59) * mm, "end": v(-14.29, 1.59) * mm});
            skLineSegment(sketch, "E8.2.1.8", {"start": v(-55.56, -1.59) * mm, "end": v(-44.45, -1.59) * mm});
            skLineSegment(sketch, "E8.2.1.9", {"start": v(-44.45, 1.59) * mm, "end": v(-44.45, -1.59) * mm});
            skLineSegment(sketch, "E8.2.1.10", {"start": v(-34.93, 1.59) * mm, "end": v(-34.93, -1.59) * mm});
            skLineSegment(sketch, "E8.2.1.11", {"start": v(-55.56, 1.59) * mm, "end": v(-55.56, -1.59) * mm});
            skLineSegment(sketch, "E8.2.1.12", {"start": v(-77.79, 1.59) * mm, "end": v(-77.79, -1.59) * mm});
            skLineSegment(sketch, "E8.2.1.13", {"start": v(-14.29, 1.59) * mm, "end": v(-14.29, -1.59) * mm});
            skLineSegment(sketch, "E8.2.1.14", {"start": v(-65.09, 1.59) * mm, "end": v(-65.09, -1.59) * mm});
            skLineSegment(sketch, "E8.2.1.15", {"start": v(-1.59, 1.59) * mm, "end": v(-1.59, -1.59) * mm});
            skLineSegment(sketch, "E8.2.1.16", {"start": v(-23.81, 1.59) * mm, "end": v(-23.81, -1.59) * mm});
            skLineSegment(sketch, "E8.2.2.0", {"start": v(-55.56, -77.79) * mm, "end": v(-44.45, -77.79) * mm});
            skLineSegment(sketch, "E8.2.2.1", {"start": v(-34.93, -80.96) * mm, "end": v(-23.81, -80.96) * mm});
            skLineSegment(sketch, "E8.2.2.2", {"start": v(-55.56, -80.96) * mm, "end": v(-34.93, -80.96) * mm, "construction": true});
            skLineSegment(sketch, "E8.2.2.3", {"start": v(-34.93, -77.79) * mm, "end": v(-23.81, -77.79) * mm});
            skLineSegment(sketch, "E8.2.2.4", {"start": v(-1.59, -80.96) * mm, "end": v(-14.29, -80.96) * mm});
            skLineSegment(sketch, "E8.2.2.5", {"start": v(-77.79, -80.96) * mm, "end": v(-65.09, -80.96) * mm});
            skLineSegment(sketch, "E8.2.2.6", {"start": v(-77.79, -77.79) * mm, "end": v(-65.09, -77.79) * mm});
            skLineSegment(sketch, "E8.2.2.7", {"start": v(-1.59, -77.79) * mm, "end": v(-14.29, -77.79) * mm});
            skLineSegment(sketch, "E8.2.2.8", {"start": v(-55.56, -80.96) * mm, "end": v(-44.45, -80.96) * mm});
            skLineSegment(sketch, "E8.2.2.9", {"start": v(-44.45, -77.79) * mm, "end": v(-44.45, -80.96) * mm});
            skLineSegment(sketch, "E8.2.2.10", {"start": v(-34.93, -77.79) * mm, "end": v(-34.93, -80.96) * mm});
            skLineSegment(sketch, "E8.2.2.11", {"start": v(-55.56, -77.79) * mm, "end": v(-55.56, -80.96) * mm});
            skLineSegment(sketch, "E8.2.2.12", {"start": v(-77.79, -77.79) * mm, "end": v(-77.79, -80.96) * mm});
            skLineSegment(sketch, "E8.2.2.13", {"start": v(-14.29, -77.79) * mm, "end": v(-14.29, -80.96) * mm});
            skLineSegment(sketch, "E8.2.2.14", {"start": v(-65.09, -77.79) * mm, "end": v(-65.09, -80.96) * mm});
            skLineSegment(sketch, "E8.2.2.15", {"start": v(-1.59, -77.79) * mm, "end": v(-1.59, -80.96) * mm});
            skLineSegment(sketch, "E8.2.2.16", {"start": v(-23.81, -77.79) * mm, "end": v(-23.81, -80.96) * mm});
            skLineSegment(sketch, "E8.3.0.0", {"start": v(23.81, 80.96) * mm, "end": v(34.92, 80.96) * mm});
            skLineSegment(sketch, "E8.3.0.1", {"start": v(44.45, 77.79) * mm, "end": v(55.56, 77.79) * mm});
            skLineSegment(sketch, "E8.3.0.2", {"start": v(23.81, 77.79) * mm, "end": v(44.45, 77.79) * mm, "construction": true});
            skLineSegment(sketch, "E8.3.0.3", {"start": v(44.45, 80.96) * mm, "end": v(55.56, 80.96) * mm});
            skLineSegment(sketch, "E8.3.0.4", {"start": v(77.79, 77.79) * mm, "end": v(65.09, 77.79) * mm});
            skLineSegment(sketch, "E8.3.0.5", {"start": v(1.59, 77.79) * mm, "end": v(14.29, 77.79) * mm});
            skLineSegment(sketch, "E8.3.0.6", {"start": v(1.59, 80.96) * mm, "end": v(14.29, 80.96) * mm});
            skLineSegment(sketch, "E8.3.0.7", {"start": v(77.79, 80.96) * mm, "end": v(65.09, 80.96) * mm});
            skLineSegment(sketch, "E8.3.0.8", {"start": v(23.81, 77.79) * mm, "end": v(34.92, 77.79) * mm});
            skLineSegment(sketch, "E8.3.0.9", {"start": v(34.92, 80.96) * mm, "end": v(34.92, 77.79) * mm});
            skLineSegment(sketch, "E8.3.0.10", {"start": v(44.45, 80.96) * mm, "end": v(44.45, 77.79) * mm});
            skLineSegment(sketch, "E8.3.0.11", {"start": v(23.81, 80.96) * mm, "end": v(23.81, 77.79) * mm});
            skLineSegment(sketch, "E8.3.0.12", {"start": v(1.59, 80.96) * mm, "end": v(1.59, 77.79) * mm});
            skLineSegment(sketch, "E8.3.0.13", {"start": v(65.09, 80.96) * mm, "end": v(65.09, 77.79) * mm});
            skLineSegment(sketch, "E8.3.0.14", {"start": v(14.29, 80.96) * mm, "end": v(14.29, 77.79) * mm});
            skLineSegment(sketch, "E8.3.0.15", {"start": v(77.79, 80.96) * mm, "end": v(77.79, 77.79) * mm});
            skLineSegment(sketch, "E8.3.0.16", {"start": v(55.56, 80.96) * mm, "end": v(55.56, 77.79) * mm});
            skLineSegment(sketch, "E8.3.1.0", {"start": v(23.81, 1.59) * mm, "end": v(34.92, 1.59) * mm});
            skLineSegment(sketch, "E8.3.1.1", {"start": v(44.45, -1.59) * mm, "end": v(55.56, -1.59) * mm});
            skLineSegment(sketch, "E8.3.1.2", {"start": v(23.81, -1.59) * mm, "end": v(44.45, -1.59) * mm, "construction": true});
            skLineSegment(sketch, "E8.3.1.3", {"start": v(44.45, 1.59) * mm, "end": v(55.56, 1.59) * mm});
            skLineSegment(sketch, "E8.3.1.4", {"start": v(77.79, -1.59) * mm, "end": v(65.09, -1.59) * mm});
            skLineSegment(sketch, "E8.3.1.5", {"start": v(1.59, -1.59) * mm, "end": v(14.29, -1.59) * mm});
            skLineSegment(sketch, "E8.3.1.6", {"start": v(1.59, 1.59) * mm, "end": v(14.29, 1.59) * mm});
            skLineSegment(sketch, "E8.3.1.7", {"start": v(77.79, 1.59) * mm, "end": v(65.09, 1.59) * mm});
            skLineSegment(sketch, "E8.3.1.8", {"start": v(23.81, -1.59) * mm, "end": v(34.92, -1.59) * mm});
            skLineSegment(sketch, "E8.3.1.9", {"start": v(34.92, 1.59) * mm, "end": v(34.92, -1.59) * mm});
            skLineSegment(sketch, "E8.3.1.10", {"start": v(44.45, 1.59) * mm, "end": v(44.45, -1.59) * mm});
            skLineSegment(sketch, "E8.3.1.11", {"start": v(23.81, 1.59) * mm, "end": v(23.81, -1.59) * mm});
            skLineSegment(sketch, "E8.3.1.12", {"start": v(1.59, 1.59) * mm, "end": v(1.59, -1.59) * mm});
            skLineSegment(sketch, "E8.3.1.13", {"start": v(65.09, 1.59) * mm, "end": v(65.09, -1.59) * mm});
            skLineSegment(sketch, "E8.3.1.14", {"start": v(14.29, 1.59) * mm, "end": v(14.29, -1.59) * mm});
            skLineSegment(sketch, "E8.3.1.15", {"start": v(77.79, 1.59) * mm, "end": v(77.79, -1.59) * mm});
            skLineSegment(sketch, "E8.3.1.16", {"start": v(55.56, 1.59) * mm, "end": v(55.56, -1.59) * mm});
            skLineSegment(sketch, "E8.3.2.0", {"start": v(23.81, -77.79) * mm, "end": v(34.92, -77.79) * mm});
            skLineSegment(sketch, "E8.3.2.1", {"start": v(44.45, -80.96) * mm, "end": v(55.56, -80.96) * mm});
            skLineSegment(sketch, "E8.3.2.2", {"start": v(23.81, -80.96) * mm, "end": v(44.45, -80.96) * mm, "construction": true});
            skLineSegment(sketch, "E8.3.2.3", {"start": v(44.45, -77.79) * mm, "end": v(55.56, -77.79) * mm});
            skLineSegment(sketch, "E8.3.2.4", {"start": v(77.79, -80.96) * mm, "end": v(65.09, -80.96) * mm});
            skLineSegment(sketch, "E8.3.2.5", {"start": v(1.59, -80.96) * mm, "end": v(14.29, -80.96) * mm});
            skLineSegment(sketch, "E8.3.2.6", {"start": v(1.59, -77.79) * mm, "end": v(14.29, -77.79) * mm});
            skLineSegment(sketch, "E8.3.2.7", {"start": v(77.79, -77.79) * mm, "end": v(65.09, -77.79) * mm});
            skLineSegment(sketch, "E8.3.2.8", {"start": v(23.81, -80.96) * mm, "end": v(34.92, -80.96) * mm});
            skLineSegment(sketch, "E8.3.2.9", {"start": v(34.92, -77.79) * mm, "end": v(34.92, -80.96) * mm});
            skLineSegment(sketch, "E8.3.2.10", {"start": v(44.45, -77.79) * mm, "end": v(44.45, -80.96) * mm});
            skLineSegment(sketch, "E8.3.2.11", {"start": v(23.81, -77.79) * mm, "end": v(23.81, -80.96) * mm});
            skLineSegment(sketch, "E8.3.2.12", {"start": v(1.59, -77.79) * mm, "end": v(1.59, -80.96) * mm});
            skLineSegment(sketch, "E8.3.2.13", {"start": v(65.09, -77.79) * mm, "end": v(65.09, -80.96) * mm});
            skLineSegment(sketch, "E8.3.2.14", {"start": v(14.29, -77.79) * mm, "end": v(14.29, -80.96) * mm});
            skLineSegment(sketch, "E8.3.2.15", {"start": v(77.79, -77.79) * mm, "end": v(77.79, -80.96) * mm});
            skLineSegment(sketch, "E8.3.2.16", {"start": v(55.56, -77.79) * mm, "end": v(55.56, -80.96) * mm});
            skLineSegment(sketch, "E8.4.0.0", {"start": v(103.19, 80.96) * mm, "end": v(114.3, 80.96) * mm});
            skLineSegment(sketch, "E8.4.0.1", {"start": v(123.82, 77.79) * mm, "end": v(134.94, 77.79) * mm});
            skLineSegment(sketch, "E8.4.0.2", {"start": v(103.19, 77.79) * mm, "end": v(123.82, 77.79) * mm, "construction": true});
            skLineSegment(sketch, "E8.4.0.3", {"start": v(123.82, 80.96) * mm, "end": v(134.94, 80.96) * mm});
            skLineSegment(sketch, "E8.4.0.4", {"start": v(157.16, 77.79) * mm, "end": v(144.46, 77.79) * mm});
            skLineSegment(sketch, "E8.4.0.5", {"start": v(80.96, 77.79) * mm, "end": v(93.66, 77.79) * mm});
            skLineSegment(sketch, "E8.4.0.6", {"start": v(80.96, 80.96) * mm, "end": v(93.66, 80.96) * mm});
            skLineSegment(sketch, "E8.4.0.7", {"start": v(157.16, 80.96) * mm, "end": v(144.46, 80.96) * mm});
            skLineSegment(sketch, "E8.4.0.8", {"start": v(103.19, 77.79) * mm, "end": v(114.3, 77.79) * mm});
            skLineSegment(sketch, "E8.4.0.9", {"start": v(114.3, 80.96) * mm, "end": v(114.3, 77.79) * mm});
            skLineSegment(sketch, "E8.4.0.10", {"start": v(123.82, 80.96) * mm, "end": v(123.82, 77.79) * mm});
            skLineSegment(sketch, "E8.4.0.11", {"start": v(103.19, 80.96) * mm, "end": v(103.19, 77.79) * mm});
            skLineSegment(sketch, "E8.4.0.12", {"start": v(80.96, 80.96) * mm, "end": v(80.96, 77.79) * mm});
            skLineSegment(sketch, "E8.4.0.13", {"start": v(144.46, 80.96) * mm, "end": v(144.46, 77.79) * mm});
            skLineSegment(sketch, "E8.4.0.14", {"start": v(93.66, 80.96) * mm, "end": v(93.66, 77.79) * mm});
            skLineSegment(sketch, "E8.4.0.15", {"start": v(157.16, 80.96) * mm, "end": v(157.16, 77.79) * mm});
            skLineSegment(sketch, "E8.4.0.16", {"start": v(134.94, 80.96) * mm, "end": v(134.94, 77.79) * mm});
            skLineSegment(sketch, "E8.4.1.0", {"start": v(103.19, 1.59) * mm, "end": v(114.3, 1.59) * mm});
            skLineSegment(sketch, "E8.4.1.1", {"start": v(123.82, -1.59) * mm, "end": v(134.94, -1.59) * mm});
            skLineSegment(sketch, "E8.4.1.2", {"start": v(103.19, -1.59) * mm, "end": v(123.82, -1.59) * mm, "construction": true});
            skLineSegment(sketch, "E8.4.1.3", {"start": v(123.82, 1.59) * mm, "end": v(134.94, 1.59) * mm});
            skLineSegment(sketch, "E8.4.1.4", {"start": v(157.16, -1.59) * mm, "end": v(144.46, -1.59) * mm});
            skLineSegment(sketch, "E8.4.1.5", {"start": v(80.96, -1.59) * mm, "end": v(93.66, -1.59) * mm});
            skLineSegment(sketch, "E8.4.1.6", {"start": v(80.96, 1.59) * mm, "end": v(93.66, 1.59) * mm});
            skLineSegment(sketch, "E8.4.1.7", {"start": v(157.16, 1.59) * mm, "end": v(144.46, 1.59) * mm});
            skLineSegment(sketch, "E8.4.1.8", {"start": v(103.19, -1.59) * mm, "end": v(114.3, -1.59) * mm});
            skLineSegment(sketch, "E8.4.1.9", {"start": v(114.3, 1.59) * mm, "end": v(114.3, -1.59) * mm});
            skLineSegment(sketch, "E8.4.1.10", {"start": v(123.82, 1.59) * mm, "end": v(123.82, -1.59) * mm});
            skLineSegment(sketch, "E8.4.1.11", {"start": v(103.19, 1.59) * mm, "end": v(103.19, -1.59) * mm});
            skLineSegment(sketch, "E8.4.1.12", {"start": v(80.96, 1.59) * mm, "end": v(80.96, -1.59) * mm});
            skLineSegment(sketch, "E8.4.1.13", {"start": v(144.46, 1.59) * mm, "end": v(144.46, -1.59) * mm});
            skLineSegment(sketch, "E8.4.1.14", {"start": v(93.66, 1.59) * mm, "end": v(93.66, -1.59) * mm});
            skLineSegment(sketch, "E8.4.1.15", {"start": v(157.16, 1.59) * mm, "end": v(157.16, -1.59) * mm});
            skLineSegment(sketch, "E8.4.1.16", {"start": v(134.94, 1.59) * mm, "end": v(134.94, -1.59) * mm});
            skLineSegment(sketch, "E8.4.2.0", {"start": v(103.19, -77.79) * mm, "end": v(114.3, -77.79) * mm});
            skLineSegment(sketch, "E8.4.2.1", {"start": v(123.82, -80.96) * mm, "end": v(134.94, -80.96) * mm});
            skLineSegment(sketch, "E8.4.2.2", {"start": v(103.19, -80.96) * mm, "end": v(123.82, -80.96) * mm, "construction": true});
            skLineSegment(sketch, "E8.4.2.3", {"start": v(123.82, -77.79) * mm, "end": v(134.94, -77.79) * mm});
            skLineSegment(sketch, "E8.4.2.4", {"start": v(157.16, -80.96) * mm, "end": v(144.46, -80.96) * mm});
            skLineSegment(sketch, "E8.4.2.5", {"start": v(80.96, -80.96) * mm, "end": v(93.66, -80.96) * mm});
            skLineSegment(sketch, "E8.4.2.6", {"start": v(80.96, -77.79) * mm, "end": v(93.66, -77.79) * mm});
            skLineSegment(sketch, "E8.4.2.7", {"start": v(157.16, -77.79) * mm, "end": v(144.46, -77.79) * mm});
            skLineSegment(sketch, "E8.4.2.8", {"start": v(103.19, -80.96) * mm, "end": v(114.3, -80.96) * mm});
            skLineSegment(sketch, "E8.4.2.9", {"start": v(114.3, -77.79) * mm, "end": v(114.3, -80.96) * mm});
            skLineSegment(sketch, "E8.4.2.10", {"start": v(123.82, -77.79) * mm, "end": v(123.82, -80.96) * mm});
            skLineSegment(sketch, "E8.4.2.11", {"start": v(103.19, -77.79) * mm, "end": v(103.19, -80.96) * mm});
            skLineSegment(sketch, "E8.4.2.12", {"start": v(80.96, -77.79) * mm, "end": v(80.96, -80.96) * mm});
            skLineSegment(sketch, "E8.4.2.13", {"start": v(144.46, -77.79) * mm, "end": v(144.46, -80.96) * mm});
            skLineSegment(sketch, "E8.4.2.14", {"start": v(93.66, -77.79) * mm, "end": v(93.66, -80.96) * mm});
            skLineSegment(sketch, "E8.4.2.15", {"start": v(157.16, -77.79) * mm, "end": v(157.16, -80.96) * mm});
            skLineSegment(sketch, "E8.4.2.16", {"start": v(134.94, -77.79) * mm, "end": v(134.94, -80.96) * mm});
            skLineSegment(sketch, "E8.5.0.0", {"start": v(182.56, 80.96) * mm, "end": v(193.67, 80.96) * mm});
            skLineSegment(sketch, "E8.5.0.1", {"start": v(203.2, 77.79) * mm, "end": v(214.31, 77.79) * mm});
            skLineSegment(sketch, "E8.5.0.2", {"start": v(182.56, 77.79) * mm, "end": v(203.2, 77.79) * mm, "construction": true});
            skLineSegment(sketch, "E8.5.0.3", {"start": v(203.2, 80.96) * mm, "end": v(214.31, 80.96) * mm});
            skLineSegment(sketch, "E8.5.0.4", {"start": v(236.54, 77.79) * mm, "end": v(223.84, 77.79) * mm});
            skLineSegment(sketch, "E8.5.0.5", {"start": v(160.34, 77.79) * mm, "end": v(173.04, 77.79) * mm});
            skLineSegment(sketch, "E8.5.0.6", {"start": v(160.34, 80.96) * mm, "end": v(173.04, 80.96) * mm});
            skLineSegment(sketch, "E8.5.0.7", {"start": v(236.54, 80.96) * mm, "end": v(223.84, 80.96) * mm});
            skLineSegment(sketch, "E8.5.0.8", {"start": v(182.56, 77.79) * mm, "end": v(193.67, 77.79) * mm});
            skLineSegment(sketch, "E8.5.0.9", {"start": v(193.67, 80.96) * mm, "end": v(193.67, 77.79) * mm});
            skLineSegment(sketch, "E8.5.0.10", {"start": v(203.2, 80.96) * mm, "end": v(203.2, 77.79) * mm});
            skLineSegment(sketch, "E8.5.0.11", {"start": v(182.56, 80.96) * mm, "end": v(182.56, 77.79) * mm});
            skLineSegment(sketch, "E8.5.0.12", {"start": v(160.34, 80.96) * mm, "end": v(160.34, 77.79) * mm});
            skLineSegment(sketch, "E8.5.0.13", {"start": v(223.84, 80.96) * mm, "end": v(223.84, 77.79) * mm});
            skLineSegment(sketch, "E8.5.0.14", {"start": v(173.04, 80.96) * mm, "end": v(173.04, 77.79) * mm});
            skLineSegment(sketch, "E8.5.0.15", {"start": v(236.54, 80.96) * mm, "end": v(236.54, 77.79) * mm});
            skLineSegment(sketch, "E8.5.0.16", {"start": v(214.31, 80.96) * mm, "end": v(214.31, 77.79) * mm});
            skLineSegment(sketch, "E8.5.1.0", {"start": v(182.56, 1.59) * mm, "end": v(193.67, 1.59) * mm});
            skLineSegment(sketch, "E8.5.1.1", {"start": v(203.2, -1.59) * mm, "end": v(214.31, -1.59) * mm});
            skLineSegment(sketch, "E8.5.1.2", {"start": v(182.56, -1.59) * mm, "end": v(203.2, -1.59) * mm, "construction": true});
            skLineSegment(sketch, "E8.5.1.3", {"start": v(203.2, 1.59) * mm, "end": v(214.31, 1.59) * mm});
            skLineSegment(sketch, "E8.5.1.4", {"start": v(236.54, -1.59) * mm, "end": v(223.84, -1.59) * mm});
            skLineSegment(sketch, "E8.5.1.5", {"start": v(160.34, -1.59) * mm, "end": v(173.04, -1.59) * mm});
            skLineSegment(sketch, "E8.5.1.6", {"start": v(160.34, 1.59) * mm, "end": v(173.04, 1.59) * mm});
            skLineSegment(sketch, "E8.5.1.7", {"start": v(236.54, 1.59) * mm, "end": v(223.84, 1.59) * mm});
            skLineSegment(sketch, "E8.5.1.8", {"start": v(182.56, -1.59) * mm, "end": v(193.67, -1.59) * mm});
            skLineSegment(sketch, "E8.5.1.9", {"start": v(193.67, 1.59) * mm, "end": v(193.67, -1.59) * mm});
            skLineSegment(sketch, "E8.5.1.10", {"start": v(203.2, 1.59) * mm, "end": v(203.2, -1.59) * mm});
            skLineSegment(sketch, "E8.5.1.11", {"start": v(182.56, 1.59) * mm, "end": v(182.56, -1.59) * mm});
            skLineSegment(sketch, "E8.5.1.12", {"start": v(160.34, 1.59) * mm, "end": v(160.34, -1.59) * mm});
            skLineSegment(sketch, "E8.5.1.13", {"start": v(223.84, 1.59) * mm, "end": v(223.84, -1.59) * mm});
            skLineSegment(sketch, "E8.5.1.14", {"start": v(173.04, 1.59) * mm, "end": v(173.04, -1.59) * mm});
            skLineSegment(sketch, "E8.5.1.15", {"start": v(236.54, 1.59) * mm, "end": v(236.54, -1.59) * mm});
            skLineSegment(sketch, "E8.5.1.16", {"start": v(214.31, 1.59) * mm, "end": v(214.31, -1.59) * mm});
            skLineSegment(sketch, "E8.5.2.0", {"start": v(182.56, -77.79) * mm, "end": v(193.67, -77.79) * mm});
            skLineSegment(sketch, "E8.5.2.1", {"start": v(203.2, -80.96) * mm, "end": v(214.31, -80.96) * mm});
            skLineSegment(sketch, "E8.5.2.2", {"start": v(182.56, -80.96) * mm, "end": v(203.2, -80.96) * mm, "construction": true});
            skLineSegment(sketch, "E8.5.2.3", {"start": v(203.2, -77.79) * mm, "end": v(214.31, -77.79) * mm});
            skLineSegment(sketch, "E8.5.2.4", {"start": v(236.54, -80.96) * mm, "end": v(223.84, -80.96) * mm});
            skLineSegment(sketch, "E8.5.2.5", {"start": v(160.34, -80.96) * mm, "end": v(173.04, -80.96) * mm});
            skLineSegment(sketch, "E8.5.2.6", {"start": v(160.34, -77.79) * mm, "end": v(173.04, -77.79) * mm});
            skLineSegment(sketch, "E8.5.2.7", {"start": v(236.54, -77.79) * mm, "end": v(223.84, -77.79) * mm});
            skLineSegment(sketch, "E8.5.2.8", {"start": v(182.56, -80.96) * mm, "end": v(193.67, -80.96) * mm});
            skLineSegment(sketch, "E8.5.2.9", {"start": v(193.67, -77.79) * mm, "end": v(193.67, -80.96) * mm});
            skLineSegment(sketch, "E8.5.2.10", {"start": v(203.2, -77.79) * mm, "end": v(203.2, -80.96) * mm});
            skLineSegment(sketch, "E8.5.2.11", {"start": v(182.56, -77.79) * mm, "end": v(182.56, -80.96) * mm});
            skLineSegment(sketch, "E8.5.2.12", {"start": v(160.34, -77.79) * mm, "end": v(160.34, -80.96) * mm});
            skLineSegment(sketch, "E8.5.2.13", {"start": v(223.84, -77.79) * mm, "end": v(223.84, -80.96) * mm});
            skLineSegment(sketch, "E8.5.2.14", {"start": v(173.04, -77.79) * mm, "end": v(173.04, -80.96) * mm});
            skLineSegment(sketch, "E8.5.2.15", {"start": v(236.54, -77.79) * mm, "end": v(236.54, -80.96) * mm});
            skLineSegment(sketch, "E8.5.2.16", {"start": v(214.31, -77.79) * mm, "end": v(214.31, -80.96) * mm});
            skLineSegment(sketch, "E8.direction1", {"start": v(-236.54, 77.79) * mm, "end": v(-157.16, 77.79) * mm, "construction": true});
            skLineSegment(sketch, "E8.direction2", {"start": v(-236.54, 77.79) * mm, "end": v(-236.54, -1.59) * mm, "construction": true});
            skSolve(sketch);
        }
        {
            var Q0;
            Q0 = qSketchRegion(id + "F4", true);
            extrude(context, id + "F5", {"entities" : qUnion([Q0]), "operationType" : NewBodyOperationType.REMOVE, "endBound" : BoundingType.THROUGH_ALL, "oppositeDirection" : true, "depth" : 25.4 * mm});
        }
    });
